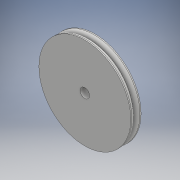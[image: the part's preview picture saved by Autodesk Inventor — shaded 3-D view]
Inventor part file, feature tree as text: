
AUTODESK INVENTOR PART (.ipt)
format: ipt  version: 2018 (Build 220112000, 112)  size: 291,328 bytes
history: native  units: mm
features: extrude x3, sketch x3, fillet x1
ambient origin geometry x8: Origin, YZ Plane, XZ Plane, XY Plane, X Axis, Y Axis, Z Axis, Center Point
bodies: Solid1 (feature_tree)
feature tree (7):
  extrude  "Extrusion1"  Depth=4.1mm
  extrude  "Extrusion2"  Depth=2.0mm
  extrude  "Extrusion3"  Depth=2.0mm TaperAngle=0.0deg
  fillet  "Fillet1"  Radius=1.5mm
  sketch  "Sketch1"  dims[d0=40.0mm d1=4.1mm]
  sketch  "Sketch2"  dims[d2=2.0mm d3=0.0mm d4=37.0mm]
  sketch  "Sketch3"  dims[d5=0.5mm d6=0.0mm d7=2.0mm d8=0.0mm d9=1.5mm]
